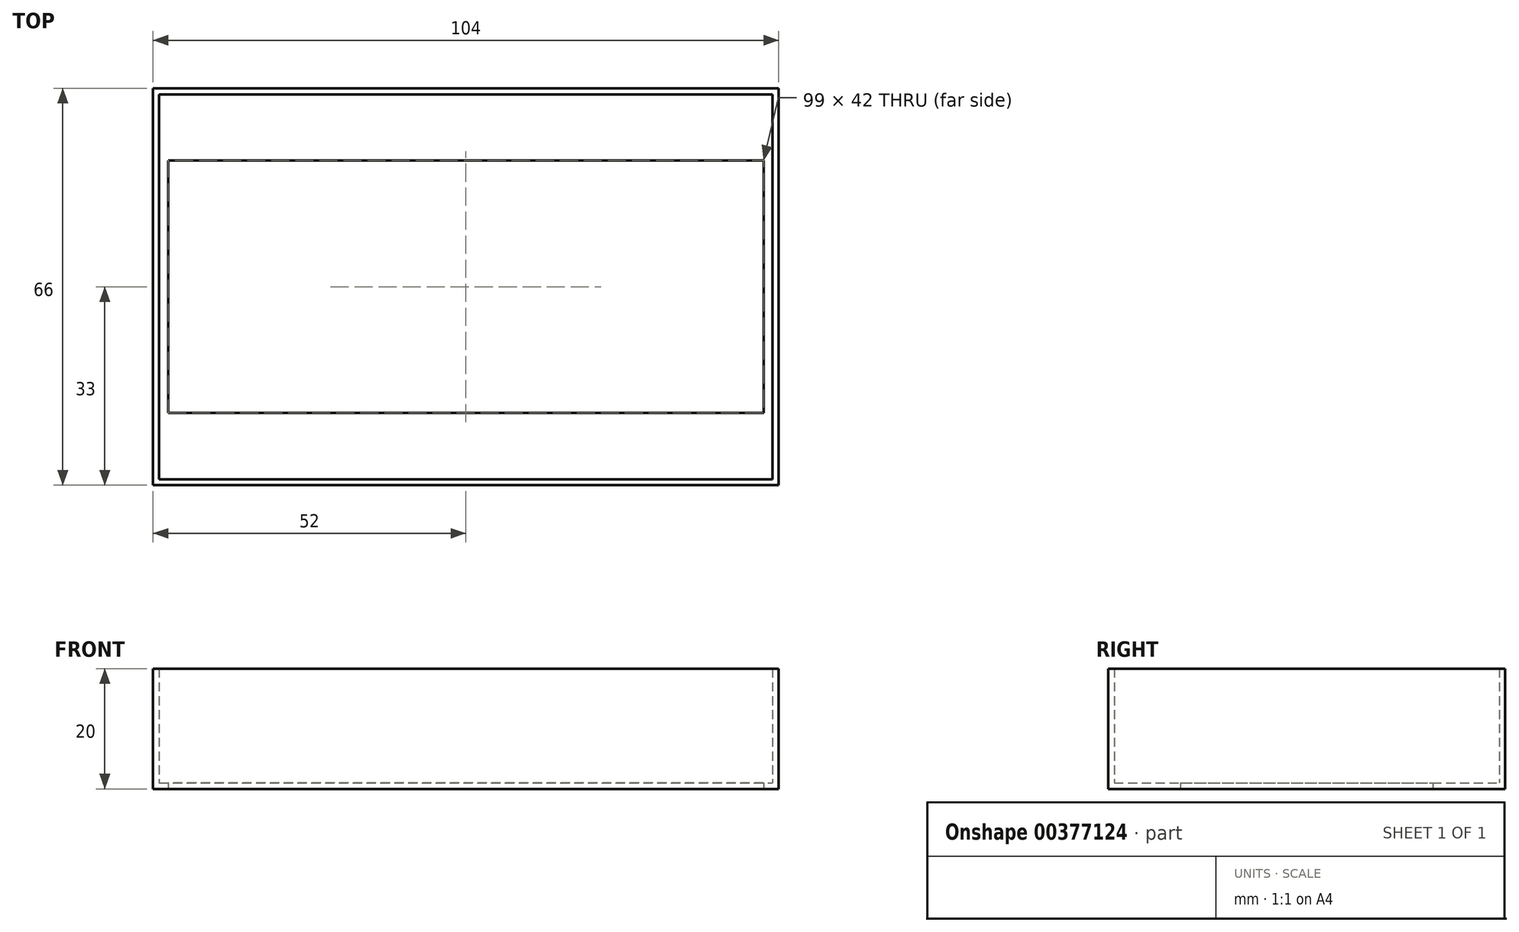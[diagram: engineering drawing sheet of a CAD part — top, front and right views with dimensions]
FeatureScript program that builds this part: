
annotation { "Feature Type Name" : "Feature", "Feature Type Description" : "" }
export const myFeature = defineFeature(function(context is Context, id is Id, definition is map)
    precondition{}
    {
        {
            var Q0;
            Q0=qCreatedBy(makeId("Top.planeOp"),FACE);
            var sketch = newSketch(context, id + "F0", { "sketchPlane" : qUnion([Q0])});
            skLineSegment(sketch, "E0.bottom", {"start": v(0, 0) * mm, "end": v(98, 0) * mm});
            skLineSegment(sketch, "E0.top", {"start": v(0, 60) * mm, "end": v(98, 60) * mm});
            skLineSegment(sketch, "E0.left", {"start": v(0, 0) * mm, "end": v(0, 60) * mm});
            skLineSegment(sketch, "E0.right", {"start": v(98, 0) * mm, "end": v(98, 60) * mm});
            skLineSegment(sketch, "E1.bottom", {"start": v(0.5, 10) * mm, "end": v(97.5, 10) * mm});
            skLineSegment(sketch, "E1.top", {"start": v(0.5, 50) * mm, "end": v(97.5, 50) * mm});
            skLineSegment(sketch, "E1.left", {"start": v(0.5, 10) * mm, "end": v(0.5, 50) * mm});
            skLineSegment(sketch, "E1.right", {"start": v(97.5, 10) * mm, "end": v(97.5, 50) * mm});
            skSolve(sketch);
        }
        {
            var Q0;
            Q0=qCreatedBy(makeId("Top.planeOp"),FACE);
            var sketch = newSketch(context, id + "F1", { "sketchPlane" : qUnion([Q0])});
            skLineSegment(sketch, "E2.0", {"start": v(98.5, 51) * mm, "end": v(-0.5, 51) * mm});
            skLineSegment(sketch, "E2.1", {"start": v(98.5, 9) * mm, "end": v(98.5, 51) * mm});
            skLineSegment(sketch, "E2.2", {"start": v(-0.5, 9) * mm, "end": v(98.5, 9) * mm});
            skLineSegment(sketch, "E2.3", {"start": v(-0.5, 51) * mm, "end": v(-0.5, 9) * mm});
            skLineSegment(sketch, "E3.0", {"start": v(100, 62) * mm, "end": v(-2, 62) * mm});
            skLineSegment(sketch, "E3.1", {"start": v(100, -2) * mm, "end": v(100, 62) * mm});
            skLineSegment(sketch, "E3.2", {"start": v(-2, -2) * mm, "end": v(100, -2) * mm});
            skLineSegment(sketch, "E3.3", {"start": v(-2, 62) * mm, "end": v(-2, -2) * mm});
            skSolve(sketch);
        }
        {
            var Q0;
            Q0=sQuery(id+"F1.wireOp",EDGE,"E3.2");
            var Q1;
            Q1=sQuery(id+"F1.wireOp",EDGE,"E3.3");
            var Q2;
            Q2=sQuery(id+"F1.wireOp",EDGE,"E3.0");
            var Q3;
            Q3=sQuery(id+"F1.wireOp",EDGE,"E3.1");
            extrude(context, id + "F2", {"bodyType" : ToolBodyType.SURFACE, "surfaceEntities" : qUnion([Q0, Q1, Q2, Q3]), "depth" : 20 * mm});
        }
        {
            var Q0;
            Q0=makeQuery(id+"F1.imprint","IMPRINT",FACE,{"disambiguationData":[TD([[makeQuery(id+"F1.imprint","IMPRINT",EDGE,{"derivedFrom":sQuery(id+"F1.wireOp",EDGE,"E2.0")}),-1.0]])]});
            var sketch = newSketch(context, id + "F3", { "sketchPlane" : qUnion([Q0])});
            skLineSegment(sketch, "E4.0", {"start": v(101, -3) * mm, "end": v(101, 63) * mm});
            skLineSegment(sketch, "E4.1", {"start": v(-3, -3) * mm, "end": v(101, -3) * mm});
            skLineSegment(sketch, "E4.2", {"start": v(-3, 63) * mm, "end": v(-3, -3) * mm});
            skLineSegment(sketch, "E4.3", {"start": v(101, 63) * mm, "end": v(-3, 63) * mm});
            skSolve(sketch);
        }
        {
            var Q0;
            Q0=makeQuery(id+"F3.imprint","IMPRINT",FACE,{"disambiguationData":[TD([[makeQuery(id+"F3.imprint","IMPRINT",EDGE,{"derivedFrom":sQuery(id+"F3.wireOp",EDGE,"E4.0")}),1.0]])]});
            extrude(context, id + "F4", {"entities" : qUnion([Q0]), "depth" : 20 * mm});
        }
        {
            var Q0;
            Q0=makeQuery(id+"F1.imprint","IMPRINT",FACE,{"disambiguationData":[TD([[makeQuery(id+"F1.imprint","IMPRINT",EDGE,{"derivedFrom":sQuery(id+"F1.wireOp",EDGE,"E2.0")}),-1.0]])]});
            extrude(context, id + "F5", {"entities" : qUnion([Q0]), "operationType" : NewBodyOperationType.ADD, "depth" : 1 * mm});
        }
    });
